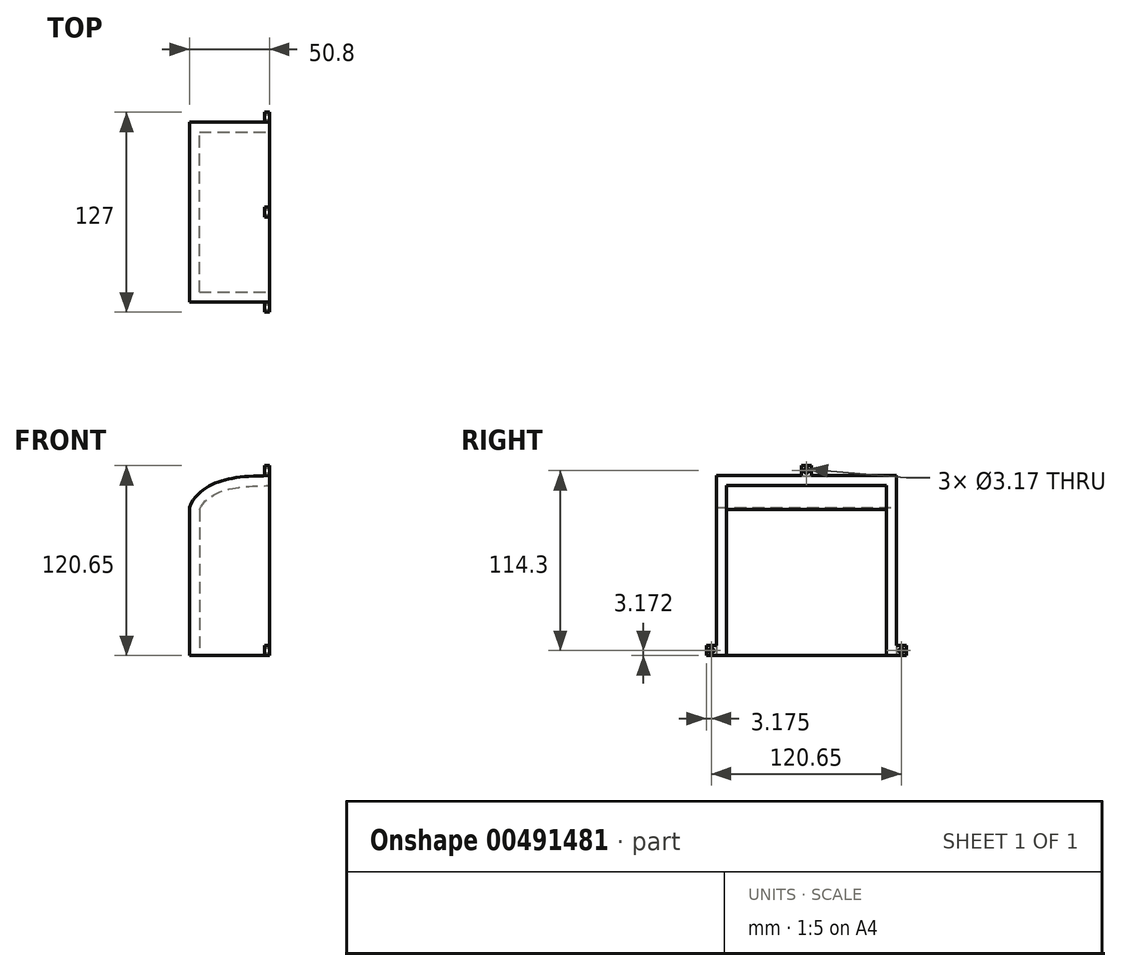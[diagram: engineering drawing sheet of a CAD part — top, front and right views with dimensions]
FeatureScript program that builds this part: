
annotation { "Feature Type Name" : "Feature", "Feature Type Description" : "" }
export const myFeature = defineFeature(function(context is Context, id is Id, definition is map)
    precondition{}
    {
        {
            var Q0;
            Q0=qCreatedBy(makeId("Front.planeOp"),FACE);
            var sketch = newSketch(context, id + "F0", { "sketchPlane" : qUnion([Q0])});
            skLineSegment(sketch, "E0", {"start": v(0, 82.98) * mm, "end": v(0, -31.32) * mm});
            skLineSegment(sketch, "E1", {"start": v(-50.8, 62.94) * mm, "end": v(-50.8, -31.32) * mm});
            skLineSegment(sketch, "E2", {"start": v(-50.8, -31.32) * mm, "end": v(0, -31.32) * mm});
            skFitSpline(sketch, "E3", {"points": [v(-50.8, 62.94) * mm, v(-33.61, 78.57) * mm, v(0, 82.98) * mm], "startDerivative": vector(24.71, 56.54) * mm, "endDerivative": vector(84.71, 0.4) * mm});
            skSolve(sketch);
        }
        {
            var Q0;
            Q0=makeQuery(id+"F0.imprint","IMPRINT",FACE,{"disambiguationData":[TD([[makeQuery(id+"F0.imprint","IMPRINT",EDGE,{"derivedFrom":sQuery(id+"F0.wireOp",EDGE,"E0")}),-1.0]])]});
            extrude(context, id + "F1", {"entities" : qUnion([Q0]), "depth" : 114.3 * mm});
        }
        {
            var Q0;
            Q0=makeQuery(id+"F1.opExtrude","SWEPT_FACE",FACE,{"disambiguationData":[OSD([sQuery(id+"F0.wireOp",EDGE,"E0")])]});
            var Q1;
            Q1=makeQuery(id+"F1.opExtrude","SWEPT_FACE",FACE,{"disambiguationData":[OSD([sQuery(id+"F0.wireOp",EDGE,"E2")])]});
            shell(context, id + "F2", {"entities" : qUnion([Q0, Q1]), "thickness" : 6.35 * mm});
        }
        {
            var Q0;
            Q0=qCreatedBy(makeId("Right.planeOp"),FACE);
            var sketch = newSketch(context, id + "F3", { "sketchPlane" : qUnion([Q0])});
            skLineSegment(sketch, "E4.bottom", {"start": v(0, -24.97) * mm, "end": v(6.35, -24.97) * mm});
            skLineSegment(sketch, "E4.top", {"start": v(0, -31.32) * mm, "end": v(6.35, -31.32) * mm});
            skLineSegment(sketch, "E4.left", {"start": v(0, -24.97) * mm, "end": v(0, -31.32) * mm});
            skLineSegment(sketch, "E4.right", {"start": v(6.35, -24.97) * mm, "end": v(6.35, -31.32) * mm});
            skCircle(sketch, "E5", {"center": v(3.18, -28.15) * mm, "radius": 1.59 * mm});
            skPoint(sketch, "E5.centerSnap0", {"position": v(0, -28.15) * mm});
            skLineSegment(sketch, "E6.bottom", {"start": v(-114.3, -24.97) * mm, "end": v(-120.65, -24.97) * mm});
            skLineSegment(sketch, "E6.top", {"start": v(-114.3, -31.32) * mm, "end": v(-120.65, -31.32) * mm});
            skLineSegment(sketch, "E6.left", {"start": v(-114.3, -24.97) * mm, "end": v(-114.3, -31.32) * mm});
            skLineSegment(sketch, "E6.right", {"start": v(-120.65, -24.97) * mm, "end": v(-120.65, -31.32) * mm});
            skCircle(sketch, "E7", {"center": v(-117.48, -28.15) * mm, "radius": 1.59 * mm});
            skPoint(sketch, "E7.centerSnap0", {"position": v(-117.48, -24.97) * mm});
            skPoint(sketch, "E7.centerSnap1", {"position": v(-114.3, -28.15) * mm});
            skLineSegment(sketch, "E8.bottom", {"start": v(-60.33, 82.98) * mm, "end": v(-53.98, 82.98) * mm, "construction": true});
            skLineSegment(sketch, "E8.top", {"start": v(-60.33, 89.33) * mm, "end": v(-53.98, 89.33) * mm});
            skLineSegment(sketch, "E8.left", {"start": v(-60.33, 82.98) * mm, "end": v(-60.33, 89.33) * mm});
            skLineSegment(sketch, "E8.right", {"start": v(-53.98, 82.98) * mm, "end": v(-53.98, 89.33) * mm});
            skCircle(sketch, "E9", {"center": v(-57.15, 86.15) * mm, "radius": 1.59 * mm});
            skPoint(sketch, "E9.centerSnap0", {"position": v(-60.33, 86.15) * mm});
            skLineSegment(sketch, "E10", {"start": v(-57.15, 82.98) * mm, "end": v(-57.15, 86.15) * mm, "construction": true});
            skLineSegment(sketch, "E11", {"start": v(0, -28.15) * mm, "end": v(3.18, -28.15) * mm, "construction": true});
            skLineSegment(sketch, "E12", {"start": v(3.18, -24.97) * mm, "end": v(3.18, -28.15) * mm, "construction": true});
            skLineSegment(sketch, "E13", {"start": v(-60.33, 82.98) * mm, "end": v(-60.33, 81.7) * mm});
            skLineSegment(sketch, "E14", {"start": v(-60.33, 81.7) * mm, "end": v(-53.98, 81.7) * mm});
            skLineSegment(sketch, "E15", {"start": v(-53.98, 81.7) * mm, "end": v(-53.98, 82.98) * mm});
            skSolve(sketch);
        }
        {
            var Q0;
            Q0 = qSketchRegion(id + "F3", true);
            extrude(context, id + "F4", {"entities" : qUnion([Q0]), "operationType" : NewBodyOperationType.ADD, "oppositeDirection" : true, "depth" : 3.17 * mm});
        }
    });
